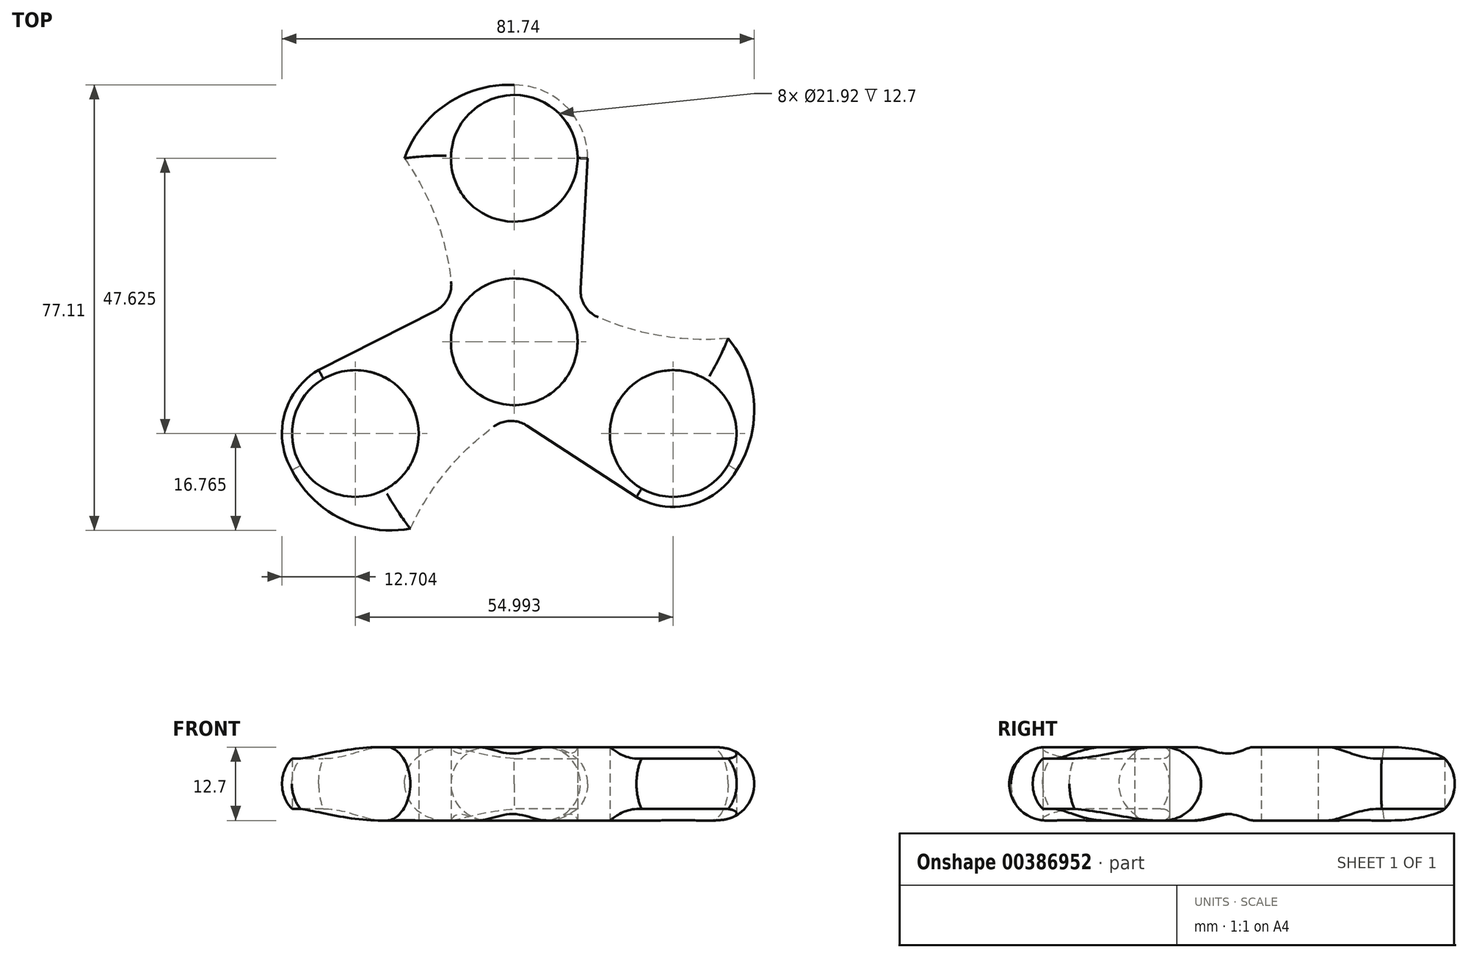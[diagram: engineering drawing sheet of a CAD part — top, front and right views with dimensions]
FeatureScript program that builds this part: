
annotation { "Feature Type Name" : "Feature", "Feature Type Description" : "" }
export const myFeature = defineFeature(function(context is Context, id is Id, definition is map)
    precondition{}
    {
        {
            var Q0;
            Q0=qCreatedBy(makeId("Top.planeOp"),FACE);
            var sketch = newSketch(context, id + "F0", { "sketchPlane" : qUnion([Q0])});
            skCircle(sketch, "E0", {"center": v(0, 0) * mm, "radius": 10.96 * mm});
            skLineSegment(sketch, "E1", {"start": v(0, 0) * mm, "end": v(0, 32.27) * mm, "construction": true});
            skCircle(sketch, "E2", {"center": v(0, 31.75) * mm, "radius": 10.96 * mm});
            skArc(sketch, "E3", {"start": v(12.63, 30.38) * mm, "mid": v(9.45, 40.23) * mm, "end": v(0, 44.45) * mm});
            skLineSegment(sketch, "E4", {"start": v(12.7, 31.75) * mm, "end": v(11.47, 9.17) * mm});
            skArc(sketch, "E5", {"start": v(0, 44.45) * mm, "mid": v(-11.6, 41.22) * mm, "end": v(-19, 31.75) * mm});
            skArc(sketch, "E6", {"start": v(-10.93, 10.45) * mm, "mid": v(-13.62, 21.6) * mm, "end": v(-19, 31.75) * mm});
            skPoint(sketch, "E7.orphan", {"position": v(-5.49, 9.5) * mm});
            skPoint(sketch, "E8.orphan", {"position": v(-5.49, -9.5) * mm});
            skArc(sketch, "E9.1.0", {"start": v(-3.58, -14.69) * mm, "mid": v(-11.9, -22.6) * mm, "end": v(-18, -32.34) * mm});
            skArc(sketch, "E9.1.1", {"start": v(-38.5, -22.22) * mm, "mid": v(-29.9, -30.65) * mm, "end": v(-18, -32.34) * mm});
            skArc(sketch, "E9.1.2", {"start": v(-32.62, -4.25) * mm, "mid": v(-39.57, -11.93) * mm, "end": v(-38.5, -22.22) * mm});
            skCircle(sketch, "E9.1.3", {"center": v(-27.5, -15.87) * mm, "radius": 10.96 * mm});
            skLineSegment(sketch, "E9.1.4", {"start": v(-33.85, -4.88) * mm, "end": v(-13.68, 5.35) * mm});
            skArc(sketch, "E9.2.0", {"start": v(14.5, 4.24) * mm, "mid": v(25.52, 1) * mm, "end": v(37, 0.59) * mm});
            skArc(sketch, "E9.2.1", {"start": v(38.5, -22.23) * mm, "mid": v(41.5, -10.57) * mm, "end": v(37, 0.59) * mm});
            skArc(sketch, "E9.2.2", {"start": v(20, -26.12) * mm, "mid": v(30.11, -28.3) * mm, "end": v(38.5, -22.23) * mm});
            skCircle(sketch, "E9.2.3", {"center": v(27.5, -15.88) * mm, "radius": 10.96 * mm});
            skLineSegment(sketch, "E9.2.4", {"start": v(21.15, -26.87) * mm, "end": v(2.2, -14.52) * mm});
            skPoint(sketch, "E10.end.orphan", {"position": v(0, 10.96) * mm});
            skPoint(sketch, "E11.newPointB", {"position": v(5.48, -9.5) * mm});
            skArc(sketch, "E11.filletArc", {"start": v(2.2, -14.52) * mm, "mid": v(-0.72, -13.7) * mm, "end": v(-3.58, -14.69) * mm});
            skPoint(sketch, "E12.newPointB", {"position": v(-10.96, 0) * mm});
            skArc(sketch, "E12.filletArc", {"start": v(-13.68, 5.35) * mm, "mid": v(-11.5, 7.47) * mm, "end": v(-10.93, 10.45) * mm});
            skPoint(sketch, "E13.newPointA", {"position": v(10.98, 0) * mm});
            skPoint(sketch, "E13.newPointB", {"position": v(5.48, 9.5) * mm});
            skArc(sketch, "E13.filletArc", {"start": v(11.47, 9.17) * mm, "mid": v(12.22, 6.23) * mm, "end": v(14.5, 4.24) * mm});
            skSolve(sketch);
        }
        {
            var Q0;
            {var subQ9=sQuery(id+"F0.wireOp",EDGE,"E9.1.1");Q0=makeQuery(id+"F0.imprint","IMPRINT",FACE,{"disambiguationData":[TD([[makeQuery(id+"F0.imprint","IMPRINT",EDGE,{"derivedFrom":subQ9}),1.0]])]});}
            var Q1;
            {var subQ8=sQuery(id+"F0.wireOp",EDGE,"E9.2.1");Q1=makeQuery(id+"F0.imprint","IMPRINT",FACE,{"disambiguationData":[TD([[makeQuery(id+"F0.imprint","IMPRINT",EDGE,{"derivedFrom":subQ8}),1.0]])]});}
            var Q2;
            Q2=makeQuery(id+"F0.imprint","IMPRINT",FACE,{"disambiguationData":[TD([[makeQuery(id+"F0.imprint","IMPRINT",EDGE,{"derivedFrom":sQuery(id+"F0.wireOp",EDGE,"E2")}),-1.0]])]});
            extrude(context, id + "F1", {"entities" : qUnion([Q0, Q1, Q2]), "depth" : 12.7 * mm});
        }
        {
            var Q0;
            Q0=makeQuery(id+"F1.opExtrude","CAP_EDGE",EDGE,{"disambiguationData":[OSD([sQuery(id+"F0.wireOp",EDGE,"E9.1.0")])],"isStart":false});
            var Q1;
            Q1=makeQuery(id+"F1.opExtrude","CAP_EDGE",EDGE,{"disambiguationData":[OSD([sQuery(id+"F0.wireOp",EDGE,"E9.1.1")])],"isStart":false});
            var Q2;
            Q2=makeQuery(id+"F1.opExtrude","CAP_EDGE",EDGE,{"disambiguationData":[OSD([sQuery(id+"F0.wireOp",EDGE,"E9.2.4")])],"isStart":false});
            var Q3;
            Q3=makeQuery(id+"F1.opExtrude","CAP_EDGE",EDGE,{"disambiguationData":[OSD([sQuery(id+"F0.wireOp",EDGE,"E9.2.2")])],"isStart":false});
            var Q4;
            Q4=makeQuery(id+"F1.opExtrude","CAP_EDGE",EDGE,{"disambiguationData":[OSD([sQuery(id+"F0.wireOp",EDGE,"E9.2.1")])],"isStart":false});
            var Q5;
            Q5=makeQuery(id+"F1.opExtrude","CAP_EDGE",EDGE,{"disambiguationData":[OSD([sQuery(id+"F0.wireOp",EDGE,"E9.2.0")])],"isStart":false});
            var Q6;
            Q6=makeQuery(id+"F1.opExtrude","CAP_EDGE",EDGE,{"disambiguationData":[OSD([sQuery(id+"F0.wireOp",EDGE,"E4")])],"isStart":false});
            var Q7;
            Q7=makeQuery(id+"F1.opExtrude","CAP_EDGE",EDGE,{"disambiguationData":[OSD([sQuery(id+"F0.wireOp",EDGE,"E3")])],"isStart":false});
            var Q8;
            Q8=makeQuery(id+"F1.opExtrude","CAP_EDGE",EDGE,{"disambiguationData":[OSD([sQuery(id+"F0.wireOp",EDGE,"E5")])],"isStart":false});
            var Q9;
            Q9=makeQuery(id+"F1.opExtrude","CAP_EDGE",EDGE,{"disambiguationData":[OSD([sQuery(id+"F0.wireOp",EDGE,"E6")])],"isStart":false});
            var Q10;
            Q10=makeQuery(id+"F1.opExtrude","CAP_EDGE",EDGE,{"disambiguationData":[OSD([sQuery(id+"F0.wireOp",EDGE,"E9.1.4")])],"isStart":false});
            var Q11;
            Q11=makeQuery(id+"F1.opExtrude","CAP_EDGE",EDGE,{"disambiguationData":[OSD([sQuery(id+"F0.wireOp",EDGE,"E9.1.2")])],"isStart":false});
            fillet(context, id + "F2", {"entities" : qUnion([Q0, Q1, Q2, Q3, Q4, Q5, Q6, Q7, Q8, Q9, Q10, Q11]), "radius" : 6.35 * mm, "tangentPropagation" : true, "allowEdgeOverflow" : false});
        }
        {
            var Q0;
            Q0=makeQuery(id+"F1.opExtrude","CAP_EDGE",EDGE,{"disambiguationData":[OSD([sQuery(id+"F0.wireOp",EDGE,"E3")])],"isStart":true});
            var Q1;
            Q1=makeQuery(id+"F1.opExtrude","CAP_EDGE",EDGE,{"disambiguationData":[OSD([sQuery(id+"F0.wireOp",EDGE,"E5")])],"isStart":true});
            var Q2;
            Q2=makeQuery(id+"F1.opExtrude","CAP_EDGE",EDGE,{"disambiguationData":[OSD([sQuery(id+"F0.wireOp",EDGE,"E6")])],"isStart":true});
            var Q3;
            Q3=makeQuery(id+"F1.opExtrude","CAP_EDGE",EDGE,{"disambiguationData":[OSD([sQuery(id+"F0.wireOp",EDGE,"E4")])],"isStart":true});
            var Q4;
            Q4=makeQuery(id+"F1.opExtrude","CAP_EDGE",EDGE,{"disambiguationData":[OSD([sQuery(id+"F0.wireOp",EDGE,"E13.filletArc")])],"isStart":true});
            var Q5;
            Q5=makeQuery(id+"F1.opExtrude","CAP_EDGE",EDGE,{"disambiguationData":[OSD([sQuery(id+"F0.wireOp",EDGE,"E9.2.0")])],"isStart":true});
            var Q6;
            Q6=makeQuery(id+"F1.opExtrude","CAP_EDGE",EDGE,{"disambiguationData":[OSD([sQuery(id+"F0.wireOp",EDGE,"E9.2.1")])],"isStart":true});
            var Q7;
            Q7=makeQuery(id+"F1.opExtrude","CAP_EDGE",EDGE,{"disambiguationData":[OSD([sQuery(id+"F0.wireOp",EDGE,"E9.2.2")])],"isStart":true});
            var Q8;
            Q8=makeQuery(id+"F1.opExtrude","CAP_EDGE",EDGE,{"disambiguationData":[OSD([sQuery(id+"F0.wireOp",EDGE,"E9.2.4")])],"isStart":true});
            var Q9;
            Q9=makeQuery(id+"F1.opExtrude","CAP_EDGE",EDGE,{"disambiguationData":[OSD([sQuery(id+"F0.wireOp",EDGE,"E9.1.0")])],"isStart":true});
            var Q10;
            Q10=makeQuery(id+"F1.opExtrude","CAP_EDGE",EDGE,{"disambiguationData":[OSD([sQuery(id+"F0.wireOp",EDGE,"E11.filletArc")])],"isStart":true});
            var Q11;
            Q11=makeQuery(id+"F1.opExtrude","CAP_EDGE",EDGE,{"disambiguationData":[OSD([sQuery(id+"F0.wireOp",EDGE,"E9.1.4")])],"isStart":true});
            var Q12;
            Q12=makeQuery(id+"F1.opExtrude","CAP_EDGE",EDGE,{"disambiguationData":[OSD([sQuery(id+"F0.wireOp",EDGE,"E12.filletArc")])],"isStart":true});
            var Q13;
            Q13=makeQuery(id+"F1.opExtrude","CAP_EDGE",EDGE,{"disambiguationData":[OSD([sQuery(id+"F0.wireOp",EDGE,"E9.1.1")])],"isStart":true});
            var Q14;
            Q14=makeQuery(id+"F1.opExtrude","CAP_EDGE",EDGE,{"disambiguationData":[OSD([sQuery(id+"F0.wireOp",EDGE,"E9.1.2")])],"isStart":true});
            fillet(context, id + "F3", {"entities" : qUnion([Q0, Q1, Q2, Q3, Q4, Q5, Q6, Q7, Q8, Q9, Q10, Q11, Q12, Q13, Q14]), "radius" : 6.35 * mm, "tangentPropagation" : true, "allowEdgeOverflow" : false});
        }
        {
            var Q0;
            Q0=makeQuery(id+"F1.opExtrude","SWEPT_BODY",BODY,{"disambiguationData":[OSD([sQuery(id+"F0.wireOp",EDGE,"E0"),sQuery(id+"F0.wireOp",EDGE,"E2"),sQuery(id+"F0.wireOp",EDGE,"E3"),sQuery(id+"F0.wireOp",EDGE,"E4"),sQuery(id+"F0.wireOp",EDGE,"E5"),sQuery(id+"F0.wireOp",EDGE,"E6"),sQuery(id+"F0.wireOp",EDGE,"E9.1.0"),sQuery(id+"F0.wireOp",EDGE,"E9.1.1"),sQuery(id+"F0.wireOp",EDGE,"E9.1.2"),sQuery(id+"F0.wireOp",EDGE,"E9.1.3"),sQuery(id+"F0.wireOp",EDGE,"E9.1.4"),sQuery(id+"F0.wireOp",EDGE,"E9.2.0"),sQuery(id+"F0.wireOp",EDGE,"E9.2.1"),sQuery(id+"F0.wireOp",EDGE,"E9.2.2"),sQuery(id+"F0.wireOp",EDGE,"E9.2.3"),sQuery(id+"F0.wireOp",EDGE,"E9.2.4"),sQuery(id+"F0.wireOp",EDGE,"E11.filletArc"),sQuery(id+"F0.wireOp",EDGE,"E12.filletArc"),sQuery(id+"F0.wireOp",EDGE,"E13.filletArc")])]});
            transform(context, id + "F4", {"entities" : qUnion([Q0]), "transformType" : TransformType.TRANSLATION_3D, "dx" : 0 * mm, "dy" : 0 * mm, "dz" : 0 * mm, "makeCopy" : true});
        }
    });
